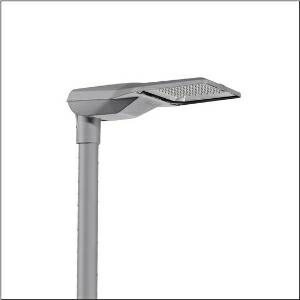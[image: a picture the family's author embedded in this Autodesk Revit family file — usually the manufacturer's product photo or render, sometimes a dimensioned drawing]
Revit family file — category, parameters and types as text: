
# Revit family: streetlight_sl_21_iq_midi___st0_8a_5xe3c31d08nb_f3e6
name_source: partatom
category: Lighting Fixtures
units: mm (PartAtom-declared; Revit-internal decimal feet)

## family parameters
Cut with Voids When Loaded = No
Host = Face
Light Source = No
Part Type = Normal
Room Calculation Point = No
Round Connector Dimension = Use Diameter
Shared = No

## types (1)
- --- (1 x LED, 23230 lm, 155.5 W, 3000K)
    Apparent Load = 155 VA
    CIE Flux Codes = 41 75 97 100 100
    Color Rendering = 70
    Color Temperature = 3000K
    Default Elevation = 1800 mm
    Description = Streetlight SL 21 iQ midi, mast luminaire, primary light control with lens, of PMMA, primary optical cover: cover, of toughened safety glass, transparent, light distribution: ST0.8a, light emission: direct distribution, primary light characteristic: asymmetric, installation type: post-top, side-entry, LED, High Power LED, rated luminous flux: 23.230lm, luminous efficacy: 149lm/W, light colour: 730, colour temperature: 3000K, control gear: iQ-Comfort, control: Auto-Match, Temp-Guard, Lumen-Switch, Night-Set, Smart-Wire, Light-Fading, Desk-Remote (wireless, voltage-free reading and setting of iQ features in the workshop via application-optimized NFC function/RFID function), optimised constant luminous flux control (CLO 2.0), pre-setting: linear dimming characteristic, mains connection: 230..240V, AC, 50/60Hz, start of lifetime: 156W, end of service life: 162W, reduction: 69W, luminaire housing, of diecast aluminium, powder-coated, Siteco® metallic grey (DB 702S), corrosivity category C5 mid according to DIN EN ISO 12944, please order mast flange separately, inclination adjustable: 0°, 5°, 10°, 15°, sealing non-destructively replaceable, multi-level sealing system, length: 644mm, width: 335mm, height: 110mm, mast flange for spigot size: 42mm (side-entry): 5XC10008XM4, 60/48mm (side-entry/post-top): 5XC10108XM2, 76/60mm (side-entry/post-top): 5XC10108XM1, mounting height: 4..8m, protection rating (complete): IP66, insulation class (complete): insulation class II (safety insulation), certification: CE, ENEC, ENEC+, VDE, impact resistance: IK10, permissible operating ambient temperature for outdoor applications: -40..+50°C, standard-compliant lighting for roads and squares, packaging unit: 1 piece

Light Distribution: ST0.8a
    Height = 111 mm
    Lamp = 1 x LED
    Lamp Light Flux = 23230 lm
    Lamp Power = 155.5 W
    Lamp count = 1
    Length = 644 mm
    Luminous efficacy = 149 lm/W
    Manufacturer = Siteco
    ModVariant = No
    Model = 5XE3C31D08NB
    Number of Poles = 1
    OnlyDefault = Yes
    Power Factor = 1
    Product Name = Streetlight SL 21 iQ midi | ST0.8a
    Product group = mast luminaire | pylon top
    ProductGroupID = 6100
    Protection Class = Protection class II
    Protection Degree = IP 66
    RLX_Detail_Level = 1
    RLX_Emergency_Light_Flux = 0 lm
    RLX_Emergency_Type = 0
    RLX_Emergency_Type_DB = No
    RlxData = <blob elided: 27265 chars, md5=4a9e9c2c>
    Socket = socket
    Standby Power = 0 W
    System Light Flux = 23230 lm
    System Power = 155 W
    Type Comments = factory setting: luminous flux: 100 % | dim-lin: 254 | 823 mA
    Type Image = l_1004298.jpg
    URL = http://relux.com
    VarID = @adj_168996
    Voltage = 0 V
    Weight = 0.00 kg
    Width = 336 mm

## geometry (parser evidence)
native form markers: Blend x4, Sweep x11
no freeform markers — native parametric forms only
